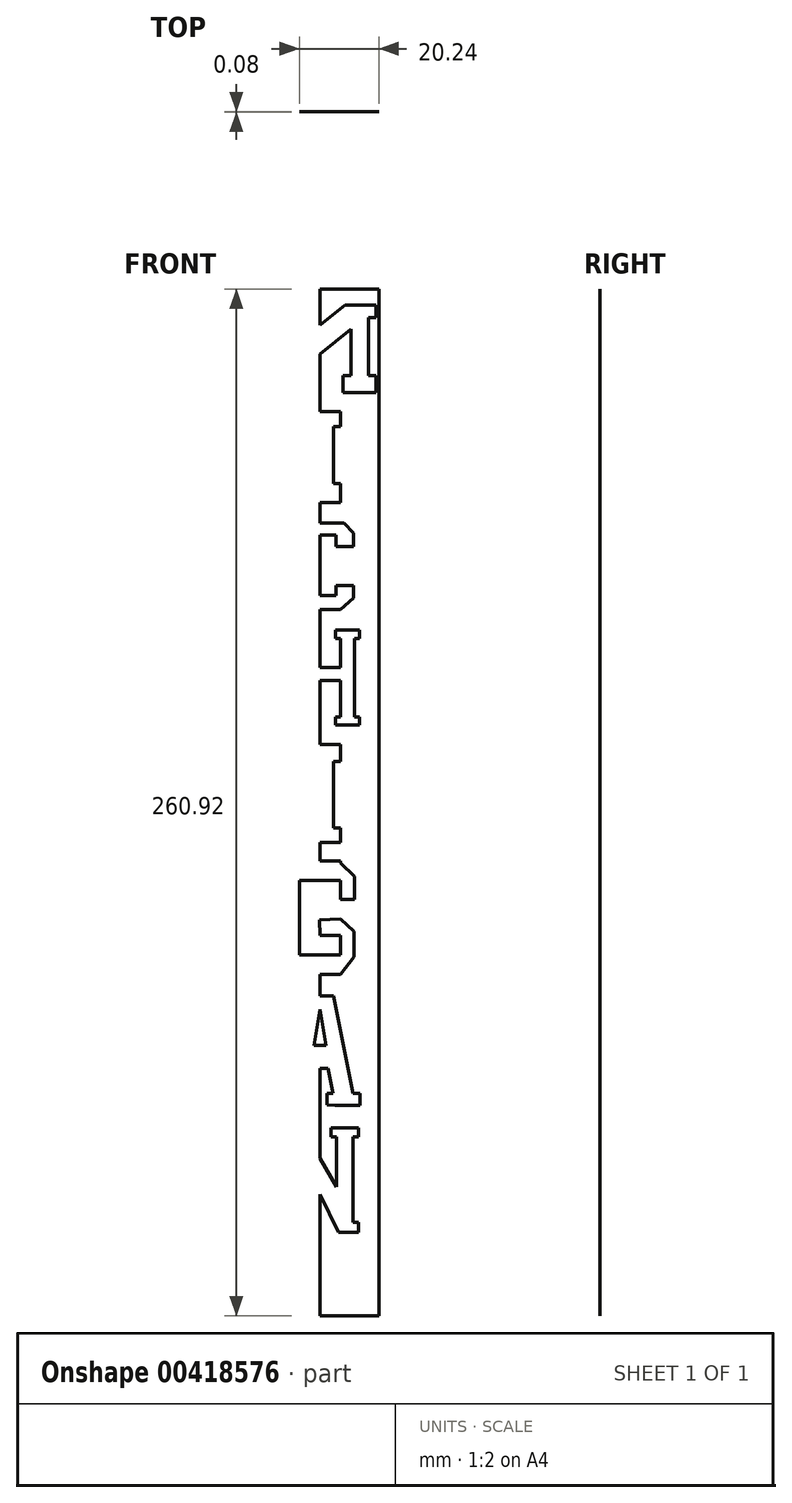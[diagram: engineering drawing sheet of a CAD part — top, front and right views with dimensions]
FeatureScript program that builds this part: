
annotation { "Feature Type Name" : "Feature", "Feature Type Description" : "" }
export const myFeature = defineFeature(function(context is Context, id is Id, definition is map)
    precondition{}
    {
        {
            var Q0;
            Q0=qCreatedBy(makeId("Front.planeOp"),FACE);
            var sketch = newSketch(context, id + "F0", { "sketchPlane" : qUnion([Q0])});
            skLineSegment(sketch, "E0.bottom", {"start": v(-64.4, 79.5) * mm, "end": v(-35.2, 79.5) * mm});
            skLineSegment(sketch, "E0.left", {"start": v(-64.4, 79.5) * mm, "end": v(-64.4, -73.46) * mm});
            skLineSegment(sketch, "E1", {"start": v(-35.2, 72.22) * mm, "end": v(-35.2, 75.43) * mm});
            skLineSegment(sketch, "E2", {"start": v(-35.2, 75.43) * mm, "end": v(-35.2, 79.5) * mm});
            skLineSegment(sketch, "E3", {"start": v(-35.2, 79.5) * mm, "end": v(-35.2, -73.46) * mm});
            skLineSegment(sketch, "E4", {"start": v(-50.2, 70.35) * mm, "end": v(-50.2, 79.5) * mm});
            skPoint(sketch, "E4.endSnap0", {"position": v(-49.3, 79.5) * mm});
            skLineSegment(sketch, "E5", {"start": v(-50.2, 79.5) * mm, "end": v(-50.2, -73.46) * mm});
            skPoint(sketch, "E5.endSnap0", {"position": v(-49.34, -73.46) * mm});
            skPoint(sketch, "E0.right.start.orphan", {"position": v(-34.18, 79.5) * mm});
            skPoint(sketch, "E6.orphan", {"position": v(-34.27, -73.46) * mm});
            skLineSegment(sketch, "E7", {"start": v(-50.2, 48.36) * mm, "end": v(-55.44, 48.36) * mm});
            skLineSegment(sketch, "E8", {"start": v(-55.44, 48.36) * mm, "end": v(-55.44, 44.52) * mm});
            skLineSegment(sketch, "E9", {"start": v(-55.44, 44.52) * mm, "end": v(-53.62, 44.52) * mm});
            skLineSegment(sketch, "E10", {"start": v(-53.62, 44.52) * mm, "end": v(-53.62, 30.02) * mm});
            skLineSegment(sketch, "E11", {"start": v(-53.62, 30.02) * mm, "end": v(-55.44, 30.02) * mm});
            skLineSegment(sketch, "E12", {"start": v(-55.44, 30.02) * mm, "end": v(-55.44, 25.22) * mm});
            skLineSegment(sketch, "E13", {"start": v(-55.44, 25.22) * mm, "end": v(-50.2, 25.22) * mm});
            skLineSegment(sketch, "E14.MirrorCS", {"start": v(-50.2, 48.36) * mm, "end": v(-44.95, 48.36) * mm});
            skLineSegment(sketch, "E15.MirrorCS", {"start": v(-44.95, 48.36) * mm, "end": v(-44.95, 44.52) * mm});
            skLineSegment(sketch, "E16.MirrorCS", {"start": v(-44.95, 44.52) * mm, "end": v(-46.77, 44.52) * mm});
            skLineSegment(sketch, "E17.MirrorCS", {"start": v(-46.77, 44.52) * mm, "end": v(-46.77, 30.02) * mm});
            skLineSegment(sketch, "E18.MirrorCS", {"start": v(-46.77, 30.02) * mm, "end": v(-44.95, 30.02) * mm});
            skLineSegment(sketch, "E19.MirrorCS", {"start": v(-44.95, 30.02) * mm, "end": v(-44.95, 25.22) * mm});
            skLineSegment(sketch, "E20.MirrorCS", {"start": v(-44.95, 25.22) * mm, "end": v(-50.2, 25.22) * mm});
            skPoint(sketch, "E21.end.orphan", {"position": v(-44.23, 75.43) * mm});
            skPoint(sketch, "E22.end.orphan", {"position": v(-37.39, 72.22) * mm});
            skPoint(sketch, "E23.start.orphan", {"position": v(-42.61, 57.47) * mm});
            skPoint(sketch, "E24.start.orphan", {"position": v(-44.63, 53.15) * mm});
            skPoint(sketch, "E25.end.orphan", {"position": v(-35.87, 57.47) * mm});
            skLineSegment(sketch, "E26.MirrorCS", {"start": v(-42.28, 69.27) * mm, "end": v(-50.2, 62.95) * mm});
            skLineSegment(sketch, "E27.MirrorCS", {"start": v(-50.2, 70.35) * mm, "end": v(-43.83, 75.43) * mm});
            skLineSegment(sketch, "E28.MirrorCS", {"start": v(-43.83, 75.43) * mm, "end": v(-35.98, 75.43) * mm});
            skLineSegment(sketch, "E29.MirrorCS", {"start": v(-35.98, 75.43) * mm, "end": v(-35.98, 72.22) * mm});
            skLineSegment(sketch, "E30.MirrorCS", {"start": v(-35.98, 72.22) * mm, "end": v(-37.87, 72.22) * mm});
            skLineSegment(sketch, "E31.MirrorCS", {"start": v(-37.87, 72.22) * mm, "end": v(-37.87, 57.47) * mm});
            skLineSegment(sketch, "E32.MirrorCS", {"start": v(-37.87, 57.47) * mm, "end": v(-35.98, 57.47) * mm});
            skLineSegment(sketch, "E33.MirrorCS", {"start": v(-35.98, 53.15) * mm, "end": v(-44.3, 53.15) * mm});
            skLineSegment(sketch, "E34.MirrorCS", {"start": v(-35.98, 57.47) * mm, "end": v(-35.98, 53.15) * mm});
            skLineSegment(sketch, "E35.MirrorCS", {"start": v(-44.3, 53.15) * mm, "end": v(-44.3, 57.47) * mm});
            skLineSegment(sketch, "E36.MirrorCS", {"start": v(-44.3, 57.47) * mm, "end": v(-42.28, 57.47) * mm});
            skLineSegment(sketch, "E37.MirrorCS", {"start": v(-42.28, 57.47) * mm, "end": v(-42.28, 69.27) * mm});
            skLineSegment(sketch, "E38", {"start": v(-50.2, 20.1) * mm, "end": v(-55.44, 20.1) * mm});
            skLineSegment(sketch, "E39", {"start": v(-55.44, 20.1) * mm, "end": v(-58.95, 16.93) * mm});
            skLineSegment(sketch, "E40", {"start": v(-58.95, 16.93) * mm, "end": v(-58.95, 1.05) * mm});
            skLineSegment(sketch, "E41", {"start": v(-58.95, 1.05) * mm, "end": v(-55.44, -2) * mm});
            skLineSegment(sketch, "E42", {"start": v(-55.44, -2) * mm, "end": v(-50.2, -2) * mm});
            skLineSegment(sketch, "E43", {"start": v(-50.2, -2) * mm, "end": v(-45, -2) * mm});
            skLineSegment(sketch, "E44", {"start": v(-45, -2) * mm, "end": v(-41.7, 0.99) * mm});
            skLineSegment(sketch, "E45", {"start": v(-41.7, 0.99) * mm, "end": v(-41.7, 4.19) * mm});
            skLineSegment(sketch, "E46", {"start": v(-41.7, 4.19) * mm, "end": v(-46.1, 4.19) * mm});
            skLineSegment(sketch, "E47", {"start": v(-46.1, 4.19) * mm, "end": v(-46.1, 1.57) * mm});
            skLineSegment(sketch, "E48", {"start": v(-46.1, 1.57) * mm, "end": v(-55.44, 1.57) * mm});
            skLineSegment(sketch, "E49", {"start": v(-55.44, 1.57) * mm, "end": v(-55.44, 16.93) * mm});
            skLineSegment(sketch, "E50", {"start": v(-55.44, 16.93) * mm, "end": v(-46.1, 16.93) * mm});
            skLineSegment(sketch, "E51", {"start": v(-46.1, 16.93) * mm, "end": v(-46.1, 14.09) * mm});
            skLineSegment(sketch, "E52", {"start": v(-46.1, 14.09) * mm, "end": v(-41.7, 14.09) * mm});
            skLineSegment(sketch, "E53", {"start": v(-41.7, 14.09) * mm, "end": v(-41.7, 17.52) * mm});
            skLineSegment(sketch, "E54", {"start": v(-41.7, 17.52) * mm, "end": v(-44.03, 20.1) * mm});
            skLineSegment(sketch, "E55", {"start": v(-44.03, 20.1) * mm, "end": v(-50.74, 20.1) * mm});
            skLineSegment(sketch, "E56", {"start": v(-58.95, -9.34) * mm, "end": v(-58.95, -29.3) * mm});
            skLineSegment(sketch, "E57", {"start": v(-58.95, -31.25) * mm, "end": v(-55.44, -31.25) * mm});
            skLineSegment(sketch, "E58", {"start": v(-55.44, -29.3) * mm, "end": v(-55.44, -19.98) * mm});
            skLineSegment(sketch, "E59", {"start": v(-55.44, -19.98) * mm, "end": v(-50.2, -19.98) * mm});
            skLineSegment(sketch, "E60", {"start": v(-50.2, -19.98) * mm, "end": v(-50.2, -16.63) * mm});
            skLineSegment(sketch, "E61", {"start": v(-50.2, -16.63) * mm, "end": v(-55.44, -16.63) * mm});
            skLineSegment(sketch, "E62", {"start": v(-55.44, -16.63) * mm, "end": v(-55.44, -9.34) * mm});
            skLineSegment(sketch, "E63", {"start": v(-55.44, -7.2) * mm, "end": v(-58.95, -7.2) * mm});
            skLineSegment(sketch, "E64.MirrorCS", {"start": v(-50.2, -16.63) * mm, "end": v(-44.95, -16.63) * mm});
            skLineSegment(sketch, "E65.MirrorCS", {"start": v(-44.95, -19.98) * mm, "end": v(-50.2, -19.98) * mm});
            skLineSegment(sketch, "E66.MirrorCS", {"start": v(-44.95, -29.3) * mm, "end": v(-44.95, -19.98) * mm});
            skLineSegment(sketch, "E67.MirrorCS", {"start": v(-41.44, -31.25) * mm, "end": v(-44.95, -31.25) * mm});
            skLineSegment(sketch, "E68.MirrorCS", {"start": v(-41.44, -9.34) * mm, "end": v(-41.44, -29.3) * mm});
            skLineSegment(sketch, "E69.MirrorCS", {"start": v(-44.95, -7.2) * mm, "end": v(-41.44, -7.2) * mm});
            skLineSegment(sketch, "E70.MirrorCS", {"start": v(-44.95, -16.63) * mm, "end": v(-44.95, -9.34) * mm});
            skLineSegment(sketch, "E71", {"start": v(-50.2, -36.27) * mm, "end": v(-55.44, -36.27) * mm});
            skLineSegment(sketch, "E72", {"start": v(-55.44, -36.27) * mm, "end": v(-55.44, -40.53) * mm});
            skLineSegment(sketch, "E73", {"start": v(-55.44, -40.53) * mm, "end": v(-53.62, -40.53) * mm});
            skLineSegment(sketch, "E74", {"start": v(-53.62, -40.53) * mm, "end": v(-53.62, -57.4) * mm});
            skLineSegment(sketch, "E75", {"start": v(-53.62, -57.4) * mm, "end": v(-55.44, -57.4) * mm});
            skLineSegment(sketch, "E76", {"start": v(-55.44, -57.4) * mm, "end": v(-55.44, -61.08) * mm});
            skLineSegment(sketch, "E77", {"start": v(-55.44, -61.08) * mm, "end": v(-50.2, -61.08) * mm});
            skLineSegment(sketch, "E78.MirrorCS", {"start": v(-50.2, -36.27) * mm, "end": v(-44.95, -36.27) * mm});
            skLineSegment(sketch, "E79.MirrorCS", {"start": v(-44.95, -36.27) * mm, "end": v(-44.95, -40.53) * mm});
            skLineSegment(sketch, "E80.MirrorCS", {"start": v(-44.95, -40.53) * mm, "end": v(-46.77, -40.53) * mm});
            skLineSegment(sketch, "E81.MirrorCS", {"start": v(-46.77, -40.53) * mm, "end": v(-46.77, -57.4) * mm});
            skLineSegment(sketch, "E82.MirrorCS", {"start": v(-46.77, -57.4) * mm, "end": v(-44.95, -57.4) * mm});
            skLineSegment(sketch, "E83.MirrorCS", {"start": v(-44.95, -57.4) * mm, "end": v(-44.95, -61.08) * mm});
            skLineSegment(sketch, "E84.MirrorCS", {"start": v(-44.95, -61.08) * mm, "end": v(-50.2, -61.08) * mm});
            skLineSegment(sketch, "E85", {"start": v(-50.2, -73.46) * mm, "end": v(-50.2, -181.42) * mm});
            skLineSegment(sketch, "E86", {"start": v(-64.4, -73.46) * mm, "end": v(-64.4, -181.42) * mm});
            skLineSegment(sketch, "E87", {"start": v(-35.2, -73.46) * mm, "end": v(-35.2, -181.42) * mm});
            skLineSegment(sketch, "E88", {"start": v(-64.4, -181.42) * mm, "end": v(-35.2, -181.42) * mm});
            skLineSegment(sketch, "E89", {"start": v(-44.95, -66.34) * mm, "end": v(-41.44, -69.78) * mm});
            skLineSegment(sketch, "E90", {"start": v(-41.44, -69.78) * mm, "end": v(-41.44, -75.62) * mm});
            skLineSegment(sketch, "E91", {"start": v(-41.44, -75.62) * mm, "end": v(-44.95, -75.62) * mm});
            skLineSegment(sketch, "E92", {"start": v(-44.95, -75.62) * mm, "end": v(-44.95, -70.8) * mm});
            skLineSegment(sketch, "E93", {"start": v(-44.95, -70.8) * mm, "end": v(-55.44, -70.8) * mm});
            skLineSegment(sketch, "E94", {"start": v(-55.44, -70.8) * mm, "end": v(-55.44, -89.7) * mm});
            skLineSegment(sketch, "E95", {"start": v(-55.44, -89.7) * mm, "end": v(-44.95, -89.7) * mm});
            skLineSegment(sketch, "E96", {"start": v(-44.95, -89.7) * mm, "end": v(-44.95, -84.72) * mm});
            skLineSegment(sketch, "E97", {"start": v(-44.95, -84.72) * mm, "end": v(-50.2, -84.72) * mm});
            skLineSegment(sketch, "E98", {"start": v(-50.2, -84.72) * mm, "end": v(-50.33, -80.77) * mm});
            skLineSegment(sketch, "E99", {"start": v(-50.33, -80.77) * mm, "end": v(-44.95, -80.58) * mm});
            skLineSegment(sketch, "E100", {"start": v(-44.95, -80.58) * mm, "end": v(-41.57, -83.69) * mm});
            skLineSegment(sketch, "E101", {"start": v(-41.57, -83.69) * mm, "end": v(-41.57, -90.21) * mm});
            skLineSegment(sketch, "E102", {"start": v(-41.57, -90.21) * mm, "end": v(-44.95, -94.68) * mm});
            skLineSegment(sketch, "E103", {"start": v(-44.95, -94.68) * mm, "end": v(-55.44, -94.68) * mm});
            skLineSegment(sketch, "E104", {"start": v(-55.44, -94.68) * mm, "end": v(-59.43, -90.04) * mm});
            skLineSegment(sketch, "E105", {"start": v(-59.43, -90.04) * mm, "end": v(-59.43, -70.8) * mm});
            skLineSegment(sketch, "E106", {"start": v(-59.43, -70.8) * mm, "end": v(-55.44, -65.82) * mm});
            skLineSegment(sketch, "E107", {"start": v(-55.44, -65.82) * mm, "end": v(-44.95, -65.82) * mm});
            skLineSegment(sketch, "E108", {"start": v(-50.2, -100.04) * mm, "end": v(-53.64, -100.04) * mm});
            skLineSegment(sketch, "E109", {"start": v(-53.64, -100.04) * mm, "end": v(-58.59, -124.9) * mm});
            skLineSegment(sketch, "E110", {"start": v(-59.18, -127.86) * mm, "end": v(-54.03, -127.86) * mm});
            skLineSegment(sketch, "E111", {"start": v(-53.46, -124.9) * mm, "end": v(-52.22, -118.46) * mm});
            skLineSegment(sketch, "E112", {"start": v(-52.22, -118.46) * mm, "end": v(-50.2, -118.46) * mm});
            skLineSegment(sketch, "E113", {"start": v(-50.2, -118.46) * mm, "end": v(-50.2, -112.67) * mm});
            skLineSegment(sketch, "E114", {"start": v(-50.2, -112.67) * mm, "end": v(-51.7, -112.67) * mm});
            skLineSegment(sketch, "E115", {"start": v(-51.7, -112.67) * mm, "end": v(-50.2, -103.52) * mm});
            skLineSegment(sketch, "E116", {"start": v(-50.2, -103.52) * mm, "end": v(-50.2, -100.04) * mm});
            skLineSegment(sketch, "E117.MirrorCS", {"start": v(-50.2, -112.67) * mm, "end": v(-48.68, -112.67) * mm});
            skLineSegment(sketch, "E118.MirrorCS", {"start": v(-48.16, -118.46) * mm, "end": v(-50.2, -118.46) * mm});
            skLineSegment(sketch, "E119.MirrorCS", {"start": v(-48.68, -112.67) * mm, "end": v(-50.2, -103.52) * mm});
            skLineSegment(sketch, "E120.MirrorCS", {"start": v(-50.2, -100.04) * mm, "end": v(-46.75, -100.04) * mm});
            skLineSegment(sketch, "E121.MirrorCS", {"start": v(-46.75, -100.04) * mm, "end": v(-41.8, -124.9) * mm});
            skLineSegment(sketch, "E122.MirrorCS", {"start": v(-46.93, -124.9) * mm, "end": v(-48.16, -118.46) * mm});
            skLineSegment(sketch, "E123.MirrorCS", {"start": v(-41.2, -127.86) * mm, "end": v(-46.36, -127.86) * mm});
            skLineSegment(sketch, "E124", {"start": v(-53.46, -124.9) * mm, "end": v(-51.95, -124.9) * mm});
            skLineSegment(sketch, "E125", {"start": v(-51.95, -124.9) * mm, "end": v(-51.95, -127.84) * mm});
            skLineSegment(sketch, "E126", {"start": v(-51.95, -127.84) * mm, "end": v(-54.03, -127.86) * mm});
            skLineSegment(sketch, "E127.MirrorCS", {"start": v(-46.93, -124.9) * mm, "end": v(-48.44, -124.9) * mm});
            skLineSegment(sketch, "E128.MirrorCS", {"start": v(-48.44, -127.84) * mm, "end": v(-46.36, -127.86) * mm});
            skLineSegment(sketch, "E129.MirrorCS", {"start": v(-48.44, -124.9) * mm, "end": v(-48.44, -127.84) * mm});
            skPoint(sketch, "E130.orphan", {"position": v(-46.36, -127.86) * mm});
            skLineSegment(sketch, "E131", {"start": v(-60.38, -124.9) * mm, "end": v(-60.38, -127.86) * mm});
            skLineSegment(sketch, "E132", {"start": v(-60.38, -127.86) * mm, "end": v(-59.18, -127.86) * mm});
            skLineSegment(sketch, "E133", {"start": v(-60.38, -124.9) * mm, "end": v(-58.59, -124.9) * mm});
            skLineSegment(sketch, "E134.MirrorCS", {"start": v(-40, -127.86) * mm, "end": v(-41.2, -127.86) * mm});
            skLineSegment(sketch, "E135.MirrorCS", {"start": v(-40, -124.9) * mm, "end": v(-40, -127.86) * mm});
            skLineSegment(sketch, "E136.MirrorCS", {"start": v(-40, -124.9) * mm, "end": v(-41.8, -124.9) * mm});
            skPoint(sketch, "E137.orphan", {"position": v(-41.2, -127.86) * mm});
            skLineSegment(sketch, "E138", {"start": v(-59.18, -160.1) * mm, "end": v(-54.64, -160.1) * mm});
            skLineSegment(sketch, "E139", {"start": v(-54.64, -157.66) * mm, "end": v(-54.64, -141.6) * mm});
            skLineSegment(sketch, "E140", {"start": v(-54.64, -141.6) * mm, "end": v(-45.45, -160.1) * mm});
            skLineSegment(sketch, "E141", {"start": v(-45.45, -160.1) * mm, "end": v(-41.8, -160.1) * mm});
            skLineSegment(sketch, "E142", {"start": v(-41.8, -157.66) * mm, "end": v(-41.8, -135.92) * mm});
            skLineSegment(sketch, "E143", {"start": v(-41.8, -133.64) * mm, "end": v(-46, -133.64) * mm});
            skLineSegment(sketch, "E144", {"start": v(-46, -135.92) * mm, "end": v(-46, -148.56) * mm});
            skLineSegment(sketch, "E145", {"start": v(-46, -148.56) * mm, "end": v(-54.64, -133.64) * mm});
            skLineSegment(sketch, "E146", {"start": v(-54.64, -133.64) * mm, "end": v(-59.18, -133.64) * mm});
            skLineSegment(sketch, "E147", {"start": v(-59.18, -135.93) * mm, "end": v(-59.18, -157.66) * mm});
            skLineSegment(sketch, "E148", {"start": v(-54.64, -160.1) * mm, "end": v(-53.3, -160.1) * mm});
            skLineSegment(sketch, "E149", {"start": v(-53.3, -160.1) * mm, "end": v(-53.3, -157.66) * mm});
            skLineSegment(sketch, "E150", {"start": v(-53.3, -157.66) * mm, "end": v(-54.64, -157.66) * mm});
            skLineSegment(sketch, "E151", {"start": v(-60.38, -157.66) * mm, "end": v(-60.38, -160.1) * mm});
            skLineSegment(sketch, "E152", {"start": v(-60.38, -160.1) * mm, "end": v(-59.18, -160.1) * mm});
            skLineSegment(sketch, "E153", {"start": v(-46, -133.64) * mm, "end": v(-47.34, -133.64) * mm});
            skLineSegment(sketch, "E154", {"start": v(-47.34, -133.64) * mm, "end": v(-47.34, -135.26) * mm});
            skLineSegment(sketch, "E155", {"start": v(-40.43, -135.26) * mm, "end": v(-40.43, -133.64) * mm});
            skLineSegment(sketch, "E156", {"start": v(-47.34, -135.26) * mm, "end": v(-47.34, -135.92) * mm});
            skLineSegment(sketch, "E157", {"start": v(-47.34, -135.92) * mm, "end": v(-46, -135.92) * mm});
            skLineSegment(sketch, "E158", {"start": v(-40.4, -135.92) * mm, "end": v(-40.43, -133.64) * mm});
            skLineSegment(sketch, "E159", {"start": v(-41.8, -133.64) * mm, "end": v(-40.43, -133.64) * mm});
            skLineSegment(sketch, "E160.trimOffspring", {"start": v(-41.8, -135.92) * mm, "end": v(-40.4, -135.92) * mm});
            skLineSegment(sketch, "E161.trimOffspring", {"start": v(-59.18, -157.66) * mm, "end": v(-60.38, -157.66) * mm});
            skLineSegment(sketch, "E162", {"start": v(-60.38, -135.93) * mm, "end": v(-59.18, -135.93) * mm});
            skLineSegment(sketch, "E163", {"start": v(-60.38, -135.93) * mm, "end": v(-60.38, -133.64) * mm});
            skLineSegment(sketch, "E164", {"start": v(-60.38, -133.64) * mm, "end": v(-59.18, -133.64) * mm});
            skLineSegment(sketch, "E165", {"start": v(-40.4, -157.66) * mm, "end": v(-41.8, -157.66) * mm});
            skLineSegment(sketch, "E166", {"start": v(-40.4, -157.66) * mm, "end": v(-40.4, -160.1) * mm});
            skLineSegment(sketch, "E167", {"start": v(-40.4, -160.1) * mm, "end": v(-41.8, -160.1) * mm});
            skLineSegment(sketch, "E168", {"start": v(-55.44, -7.2) * mm, "end": v(-54.2, -7.2) * mm});
            skLineSegment(sketch, "E169", {"start": v(-54.2, -7.2) * mm, "end": v(-54.2, -9.34) * mm});
            skLineSegment(sketch, "E170", {"start": v(-54.2, -9.34) * mm, "end": v(-55.44, -9.34) * mm});
            skLineSegment(sketch, "E171", {"start": v(-60.28, -9.34) * mm, "end": v(-60.28, -7.2) * mm});
            skLineSegment(sketch, "E172", {"start": v(-60.28, -7.2) * mm, "end": v(-58.95, -7.2) * mm});
            skLineSegment(sketch, "E173", {"start": v(-58.95, -29.3) * mm, "end": v(-60.28, -29.3) * mm});
            skLineSegment(sketch, "E174", {"start": v(-60.28, -29.3) * mm, "end": v(-60.28, -31.25) * mm});
            skLineSegment(sketch, "E175", {"start": v(-60.28, -31.25) * mm, "end": v(-54.2, -31.25) * mm});
            skLineSegment(sketch, "E176", {"start": v(-54.2, -31.25) * mm, "end": v(-54.2, -29.3) * mm});
            skLineSegment(sketch, "E177", {"start": v(-54.2, -29.3) * mm, "end": v(-55.44, -29.3) * mm});
            skLineSegment(sketch, "E178.MirrorCS", {"start": v(-46.19, -7.2) * mm, "end": v(-46.19, -9.34) * mm});
            skLineSegment(sketch, "E179.MirrorCS", {"start": v(-46.19, -9.34) * mm, "end": v(-44.95, -9.34) * mm});
            skLineSegment(sketch, "E180.MirrorCS", {"start": v(-44.95, -7.2) * mm, "end": v(-46.19, -7.2) * mm});
            skLineSegment(sketch, "E181.MirrorCS", {"start": v(-40.11, -9.34) * mm, "end": v(-40.11, -7.2) * mm});
            skLineSegment(sketch, "E182.MirrorCS", {"start": v(-40.11, -7.2) * mm, "end": v(-41.44, -7.2) * mm});
            skLineSegment(sketch, "E183.MirrorCS", {"start": v(-40.11, -29.3) * mm, "end": v(-40.11, -31.25) * mm});
            skLineSegment(sketch, "E184.MirrorCS", {"start": v(-41.44, -29.3) * mm, "end": v(-40.11, -29.3) * mm});
            skLineSegment(sketch, "E185.MirrorCS", {"start": v(-40.11, -31.25) * mm, "end": v(-46.19, -31.25) * mm});
            skLineSegment(sketch, "E186.MirrorCS", {"start": v(-46.19, -31.25) * mm, "end": v(-46.19, -29.3) * mm});
            skLineSegment(sketch, "E187.MirrorCS", {"start": v(-46.19, -29.3) * mm, "end": v(-44.95, -29.3) * mm});
            skLineSegment(sketch, "E188.trimOffspring", {"start": v(-58.95, -9.34) * mm, "end": v(-60.28, -9.34) * mm});
            skPoint(sketch, "E189.orphan", {"position": v(-44.95, -31.25) * mm});
            skPoint(sketch, "E190.orphan", {"position": v(-41.44, -31.25) * mm});
            skLineSegment(sketch, "E191.trimOffspring", {"start": v(-41.44, -9.34) * mm, "end": v(-40.11, -9.34) * mm});
            skPoint(sketch, "E192.orphan", {"position": v(-44.95, -7.2) * mm});
            skPoint(sketch, "E193.orphan", {"position": v(-41.44, -7.2) * mm});
            skLineSegment(sketch, "E194", {"start": v(-44.95, -65.82) * mm, "end": v(-44.95, -66.34) * mm});
            skLineSegment(sketch, "E195", {"start": v(-64.4, 53.15) * mm, "end": v(-64.4, 75.43) * mm});
            skPoint(sketch, "E196.end.orphan", {"position": v(-56.56, 75.43) * mm});
            skPoint(sketch, "E197.start.orphan", {"position": v(-64.4, 72.22) * mm});
            skPoint(sketch, "E198.start.orphan", {"position": v(-62.52, 72.22) * mm});
            skPoint(sketch, "E199.end.orphan", {"position": v(-50.2, 62.95) * mm});
            skPoint(sketch, "E199.start.orphan", {"position": v(-58.1, 69.27) * mm});
            skPoint(sketch, "E200.end.orphan", {"position": v(-58.1, 57.47) * mm});
            skPoint(sketch, "E201.orphan", {"position": v(-62.52, 57.47) * mm});
            skPoint(sketch, "E202.end.orphan", {"position": v(-56.09, 57.47) * mm});
            skPoint(sketch, "E203.orphan", {"position": v(-56.09, 53.15) * mm});
            skPoint(sketch, "E204.end.orphan", {"position": v(-63.99, 53.15) * mm});
            skPoint(sketch, "E205.end.orphan", {"position": v(-64.4, 57.47) * mm});
            skLineSegment(sketch, "E206.MirrorCS", {"start": v(-56.09, 53.15) * mm, "end": v(-56.09, 57.47) * mm});
            skLineSegment(sketch, "E207.MirrorCS", {"start": v(-64.4, 53.15) * mm, "end": v(-56.09, 53.15) * mm});
            skLineSegment(sketch, "E208.MirrorCS", {"start": v(-56.09, 57.47) * mm, "end": v(-58.1, 57.47) * mm});
            skLineSegment(sketch, "E209.MirrorCS", {"start": v(-58.1, 57.47) * mm, "end": v(-58.1, 69.27) * mm});
            skLineSegment(sketch, "E210.MirrorCS", {"start": v(-62.52, 72.22) * mm, "end": v(-62.52, 57.47) * mm});
            skLineSegment(sketch, "E211.MirrorCS", {"start": v(-62.52, 57.47) * mm, "end": v(-64.4, 57.47) * mm});
            skLineSegment(sketch, "E212.MirrorCS", {"start": v(-58.1, 69.27) * mm, "end": v(-50.2, 62.95) * mm});
            skLineSegment(sketch, "E213.MirrorCS", {"start": v(-50.2, 70.35) * mm, "end": v(-56.56, 75.43) * mm});
            skLineSegment(sketch, "E214.MirrorCS", {"start": v(-56.56, 75.43) * mm, "end": v(-64.4, 75.43) * mm});
            skLineSegment(sketch, "E215.MirrorCS", {"start": v(-64.4, 75.43) * mm, "end": v(-64.4, 72.22) * mm});
            skLineSegment(sketch, "E216.MirrorCS", {"start": v(-64.4, 72.22) * mm, "end": v(-62.52, 72.22) * mm});
            skSolve(sketch);
        }
        {
            var Q0;
            {var subQ0=sQuery(id+"F0.wireOp",EDGE,"E196");Q0=makeQuery(id+"F0.imprint","IMPRINT",FACE,{"disambiguationData":[TD([[makeQuery(id+"F0.imprint","IMPRINT",EDGE,{"derivedFrom":subQ0}),-1.0]])]});}
            var Q1;
            {var subQ28=sQuery(id+"F0.wireOp",EDGE,"eeNU5emQ-BLum-qmPS-OjP9-oRyd5eGGGo7y");Q1=makeQuery(id+"F0.imprint","IMPRINT",FACE,{"disambiguationData":[TD([[makeQuery(id+"F0.imprint","IMPRINT",EDGE,{"derivedFrom":subQ28}),-1.0]])]});}
            var Q2;
            {var subQ26=sQuery(id+"F0.wireOp",EDGE,"E14.MirrorCS");Q2=makeQuery(id+"F0.imprint","IMPRINT",FACE,{"disambiguationData":[TD([[makeQuery(id+"F0.imprint","IMPRINT",EDGE,{"derivedFrom":subQ26}),1.0]])]});}
            var Q3;
            {var subQ4=sQuery(id+"F0.wireOp",EDGE,"E96");Q3=makeQuery(id+"F0.imprint","IMPRINT",FACE,{"disambiguationData":[TD([[makeQuery(id+"F0.imprint","IMPRINT",EDGE,{"derivedFrom":subQ4}),1.0]])]});}
            var Q4;
            {var subQ0=sQuery(id+"F0.wireOp",EDGE,"E94");Q4=makeQuery(id+"F0.imprint","IMPRINT",FACE,{"disambiguationData":[TD([[makeQuery(id+"F0.imprint","IMPRINT",EDGE,{"derivedFrom":subQ0}),1.0]])]});}
            var Q5;
            {var subQ0=sQuery(id+"F0.wireOp",EDGE,"E114");Q5=makeQuery(id+"F0.imprint","IMPRINT",FACE,{"disambiguationData":[TD([[makeQuery(id+"F0.imprint","IMPRINT",EDGE,{"derivedFrom":subQ0}),-1.0]])]});}
            var Q6;
            {var subQ0=sQuery(id+"F0.wireOp",EDGE,"E117.MirrorCS");Q6=makeQuery(id+"F0.imprint","IMPRINT",FACE,{"disambiguationData":[TD([[makeQuery(id+"F0.imprint","IMPRINT",EDGE,{"derivedFrom":subQ0}),1.0]])]});}
            extrude(context, id + "F1", {"entities" : qUnion([Q0, Q1, Q2, Q3, Q4, Q5, Q6]), "depth" : 0.08 * mm});
        }
    });
